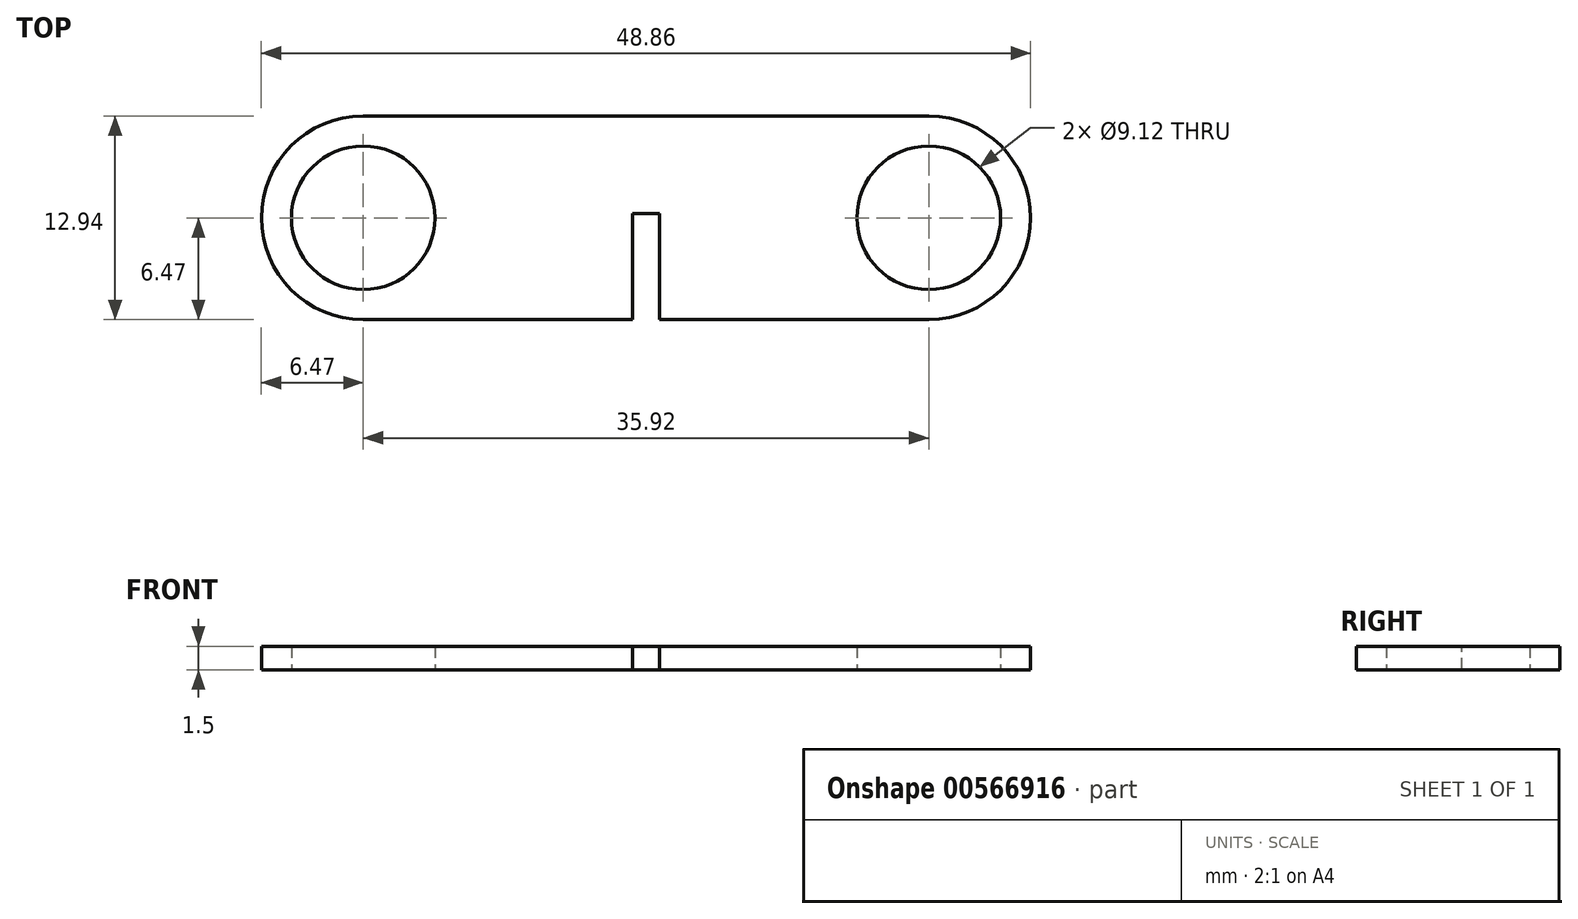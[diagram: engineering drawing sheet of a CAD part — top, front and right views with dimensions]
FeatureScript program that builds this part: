
annotation { "Feature Type Name" : "Feature", "Feature Type Description" : "" }
export const myFeature = defineFeature(function(context is Context, id is Id, definition is map)
    precondition{}
    {
        {
            var Q0;
            Q0=qCreatedBy(makeId("Top.planeOp"),FACE);
            var sketch = newSketch(context, id + "F0", { "sketchPlane" : qUnion([Q0])});
            skCircle(sketch, "E0", {"center": v(17.96, 0) * mm, "radius": 4.56 * mm});
            skCircle(sketch, "E1", {"center": v(-17.96, 0) * mm, "radius": 4.56 * mm});
            skCircle(sketch, "E2", {"center": v(-17.96, 0) * mm, "radius": 6.47 * mm});
            skCircle(sketch, "E3", {"center": v(17.96, 0) * mm, "radius": 6.47 * mm});
            skLineSegment(sketch, "E4.bottom", {"start": v(-17.96, 6.47) * mm, "end": v(17.96, 6.47) * mm});
            skLineSegment(sketch, "E4.top", {"start": v(-17.96, -6.47) * mm, "end": v(17.96, -6.47) * mm});
            skLineSegment(sketch, "E4.left", {"start": v(-17.96, 6.47) * mm, "end": v(-17.96, -6.47) * mm});
            skLineSegment(sketch, "E4.right", {"start": v(17.96, 6.47) * mm, "end": v(17.96, -6.47) * mm});
            skLineSegment(sketch, "E5.bottom", {"start": v(-4.76, 6.47) * mm, "end": v(4.76, 6.47) * mm});
            skLineSegment(sketch, "E5.top", {"start": v(-4.76, 11.3) * mm, "end": v(4.76, 11.3) * mm});
            skLineSegment(sketch, "E5.left", {"start": v(-4.76, 6.47) * mm, "end": v(-4.76, 11.3) * mm});
            skLineSegment(sketch, "E5.right", {"start": v(4.76, 6.47) * mm, "end": v(4.76, 11.3) * mm});
            skSolve(sketch);
        }
        {
            var Q0;
            Q0=makeQuery(id+"F0.imprint","IMPRINT",FACE,{"disambiguationData":[TD([[makeQuery(id+"F0.imprint","IMPRINT",EDGE,{"derivedFrom":sQuery(id+"F0.wireOp",EDGE,"E5.bottom")}),1.0]])]});
            var Q1;
            {var subQ0=sQuery(id+"F0.wireOp",EDGE,"E4.right");var subQ1=sQuery(id+"F0.wireOp",EDGE,"E0");var subQ2=makeQuery(id+"F0.imprint","INTERSECT",VERTEX,{"disambiguationData":[OD(0.0)],"derivedFrom":[subQ1,subQ0]});Q1=makeQuery(id+"F0.imprint","IMPRINT",FACE,{"disambiguationData":[TD([[makeQuery(id+"F0.imprint","IMPRINT",EDGE,{"disambiguationData":[TD([[subQ2,1.0]])],"derivedFrom":subQ1}),-1.0]])]});}
            var Q2;
            {var subQ0=sQuery(id+"F0.wireOp",EDGE,"E4.left");var subQ1=sQuery(id+"F0.wireOp",EDGE,"E1");var subQ2=makeQuery(id+"F0.imprint","INTERSECT",VERTEX,{"disambiguationData":[OD(0.0)],"derivedFrom":[subQ1,subQ0]});Q2=makeQuery(id+"F0.imprint","IMPRINT",FACE,{"disambiguationData":[TD([[makeQuery(id+"F0.imprint","IMPRINT",EDGE,{"disambiguationData":[TD([[subQ2,-1.0]])],"derivedFrom":subQ1}),-1.0]])]});}
            var Q3;
            {var subQ0=sQuery(id+"F0.wireOp",EDGE,"E4.right");var subQ1=sQuery(id+"F0.wireOp",EDGE,"E0");var subQ2=makeQuery(id+"F0.imprint","INTERSECT",VERTEX,{"disambiguationData":[OD(0.0)],"derivedFrom":[subQ1,subQ0]});Q3=makeQuery(id+"F0.imprint","IMPRINT",FACE,{"disambiguationData":[TD([[makeQuery(id+"F0.imprint","IMPRINT",EDGE,{"disambiguationData":[TD([[subQ2,-1.0]])],"derivedFrom":subQ1}),-1.0]])]});}
            var Q4;
            {var subQ0=sQuery(id+"F0.wireOp",EDGE,"E4.left");var subQ1=sQuery(id+"F0.wireOp",EDGE,"E1");var subQ2=makeQuery(id+"F0.imprint","INTERSECT",VERTEX,{"disambiguationData":[OD(0.0)],"derivedFrom":[subQ1,subQ0]});Q4=makeQuery(id+"F0.imprint","IMPRINT",FACE,{"disambiguationData":[TD([[makeQuery(id+"F0.imprint","IMPRINT",EDGE,{"disambiguationData":[TD([[subQ2,1.0]])],"derivedFrom":subQ1}),-1.0]])]});}
            var Q5;
            {var subQ8=sQuery(id+"F0.wireOp",EDGE,"E4.top");Q5=makeQuery(id+"F0.imprint","IMPRINT",FACE,{"disambiguationData":[TD([[makeQuery(id+"F0.imprint","IMPRINT",EDGE,{"derivedFrom":subQ8}),1.0]])]});}
            extrude(context, id + "F1", {"entities" : qUnion([Q0, Q1, Q2, Q3, Q4, Q5]), "depth" : 1.5 * mm, "offsetDistance" : 25.4 * mm});
        }
        {
            var Q0;
            Q0=makeQuery(id+"F1.opExtrude","CAP_FACE",FACE,{"disambiguationData":[OSD([sQuery(id+"F0.wireOp",EDGE,"E0"),sQuery(id+"F0.wireOp",EDGE,"E1"),sQuery(id+"F0.wireOp",EDGE,"E2"),sQuery(id+"F0.wireOp",EDGE,"E3"),sQuery(id+"F0.wireOp",EDGE,"E4.bottom"),sQuery(id+"F0.wireOp",EDGE,"E4.top"),sQuery(id+"F0.wireOp",EDGE,"E5.top"),sQuery(id+"F0.wireOp",EDGE,"E5.left"),sQuery(id+"F0.wireOp",EDGE,"E5.right")])],"isStart":false});
            var sketch = newSketch(context, id + "F2", { "sketchPlane" : qUnion([Q0])});
            skLineSegment(sketch, "E6.bottom", {"start": v(-0.85, -6.47) * mm, "end": v(0.85, -6.47) * mm});
            skLineSegment(sketch, "E6.top", {"start": v(-0.85, 0.26) * mm, "end": v(0.85, 0.26) * mm});
            skLineSegment(sketch, "E6.left", {"start": v(-0.85, -6.47) * mm, "end": v(-0.85, 0.26) * mm});
            skLineSegment(sketch, "E6.right", {"start": v(0.85, -6.47) * mm, "end": v(0.85, 0.26) * mm});
            skSolve(sketch);
        }
        {
            var Q0;
            Q0=makeQuery(id+"F2.imprint","IMPRINT",FACE,{"disambiguationData":[TD([[makeQuery(id+"F2.imprint","IMPRINT",EDGE,{"derivedFrom":sQuery(id+"F2.wireOp",EDGE,"E6.bottom")}),1.0]])]});
            extrude(context, id + "F3", {"entities" : qUnion([Q0]), "operationType" : NewBodyOperationType.REMOVE, "endBound" : BoundingType.THROUGH_ALL, "oppositeDirection" : true, "depth" : 25.4 * mm, "offsetDistance" : 25.4 * mm});
        }
    });
